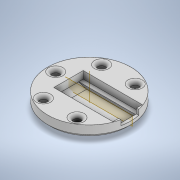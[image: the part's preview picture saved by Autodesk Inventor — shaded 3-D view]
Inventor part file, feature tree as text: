
AUTODESK INVENTOR PART (.ipt)
format: ipt  version: 2021 (Build 250183000, 183)  size: 406,016 bytes
history: native  units: in
note: dims shown in document units (in); Inventor stores cm internally (conversion verified against a paired STEP export)
features: extrude x5, sketch x5, chamfer x2, other x1, plane x1, fillet x1, pattern_circular x1
ambient origin geometry x8: Origin, YZ Plane, XZ Plane, XY Plane, X Axis, Y Axis, Z Axis, Center Point
bodies: Solid1 (feature_tree)
feature tree (16):
  extrude  "Extrusion1"  Depth=0.2835in TaperAngle=0.0deg
  chamfer  "Chamfer2"  Distance=0.1811in
  extrude  "Extrusion2"  TaperAngle=0.0deg  [1 undecoded]
  extrude  "Extrusion3"  Depth=0.1417in
  other  "Work Axis1"
  plane  "Work Plane1"
  extrude  "Extrusion5"  TaperAngle=0.0deg  [1 undecoded]
  extrude  "Extrusion4"  Depth=0.1181in
  fillet  "Fillet4"  Radius=0.2047in
  pattern_circular  "Circular Pattern2"  [2 undecoded]
  chamfer  "Chamfer3"  Distance=0.3618in
  sketch  "Sketch1"  dims[d0=2.0472in d3=0.2835in d4=0.0in]
  sketch  "Sketch2"  dims[d5=1.4551in]
  sketch  "Sketch3"  dims[d6=0.7236in]
  sketch  "Sketch4"  dims[d7=0.3618in]
  sketch  "Sketch7"  dims[d8=0.5118in d9=0.1811in d10=0.0in d11=0.0in d14=0.1417in d15=0.0in d16=0.0in d17=0.1772in d18=0.2047in d19=0.0in d23=0.8268in d24=0.3618in d28=0.5in d29=1.4in d30=0.25in d31=0.0in d32=0.063in d33=0.0in d44=0.1417in d47=0.0551in d48=0.0in d49=0.0in d51=0.0in d54=0.0787in d55=0.0in d56=45.0deg d58=0.0866in d59=0.1181in d60=1.9685in d61=240.0deg d63=0.0591in d64=0.1969in d65=45.0deg]
note: 4 required parameter values undecoded (feature->parameter linkage not recoverable at this tier; creation-order binding heuristic only, values carry confidence <= 0.55)
